# Revit family: v-180sz5(-n)_60Hz
name_source: partatom
category: 機械設備
units: mm (PartAtom-declared; Revit-internal decimal feet)

## family parameters
OmniClass タイトル = Centrifugal Fans
OmniClass 番号 = 23.75.35.17.27
パーツ タイプ = 標準
ロード時にボイドで切り取り = いいえ
丸型コネクタ寸法 = 直径を使用
作業面ベース = いいえ
共有 = いいえ
常に垂直 = はい
部屋計算ポイント = はい

## types (2) — shared parameters
Cover_Width = 120  [stored 0.393701 ft]
D1 = 369  [stored 1.21063 ft]
D2 = 120  [stored 0.393701 ft]
Depth = 304  [stored 0.997375 ft]
Duct_EA_Depth = 113  [stored 0.370735 ft]
Duct_H = 102
Duct_RA_Depth = 198  [stored 0.649606 ft]
EAサイズ_D = 98  [stored 0.321522 ft]
H1 = 25  [stored 0.082021 ft]
H2 = 157  [stored 0.515092 ft]
Height = 194  [stored 0.636483 ft]
IfcExportAs = IfcFanType
IfcExportType = PROPELLORAXIAL
MIN風量 = 60.0 m³/h
OmniClassCode = 23-33 31 19 11 15
RAサイズ_D = 98  [stored 0.321522 ft]
URL = https://www.mitsubishielectric.co.jp
Uniclass2015Code = Pr_65_67_29_12
Uniclass2015Title = Centrifugal fans
Uniclass2015Version = Systems v1.9
W1 = 369  [stored 1.21063 ft]
W2 = 110  [stored 0.360892 ft]
W3 = 152  [stored 0.498688 ft]
Width = 304  [stored 0.997375 ft]
カバーマテリアル = 合成樹脂(黒)
ダクト径 = 100 mm
ドレン管_D = 239  [stored 0.784121 ft]
ドレン管_H = 14  [stored 0.0459318 ft]
ドレン管径 = 18 mm
マテリアル = 合成樹脂(黒)
仕様書バージョン = Version1.0
企業コード = 108420
分類コード = 50052504100030
周波数 = 60 Hz
極数 = 2
法定耐用年数 = 15
点検口 = はい
点検口_Depth = 450  [stored 1.47638 ft]
点検口高さ = 20  [stored 0.0656168 ft]
相 = 1
積算_科目 = 2 換気設備
製品リリース年月 = 2022年6月1日
製品出荷対象 = 国内
製造元 = 三菱電機株式会社
設置方法 = 天埋
説明 = エアフロー環気システム サニタリー換気ユニット 中間取付形
負荷分類 = 3_ファン類
運転質量 = 0.00 kg
電動機出力 = 0 W
電圧 = 100 V

## per-type parameters (varying)
| type | MAX静圧 | MAX風量 | MID静圧 | MID風量 | MIN静圧 | 価格 | 消費電力 | 製品質量 | 質量 |
| V-180SZ5 | 100.0 Pa | 250.0 m³/h | 220.0 Pa | 120.0 m³/h | 250.0 Pa | 150200 $ | 30 W | 6.70 kg | 8.04 kg |
| V-180SZ5-N | 178.0 Pa | 225.0 m³/h | 0.0 Pa | 0.0 m³/h | 12.5 Pa | 90100 $ | 48 W | 6.00 kg | 7.20 kg |

note: column(s) folded — value = type name in every type: モデル

note: [stored X ft] marks values corroborated as IEEE doubles in the binary element streams (Revit-internal decimal feet)
